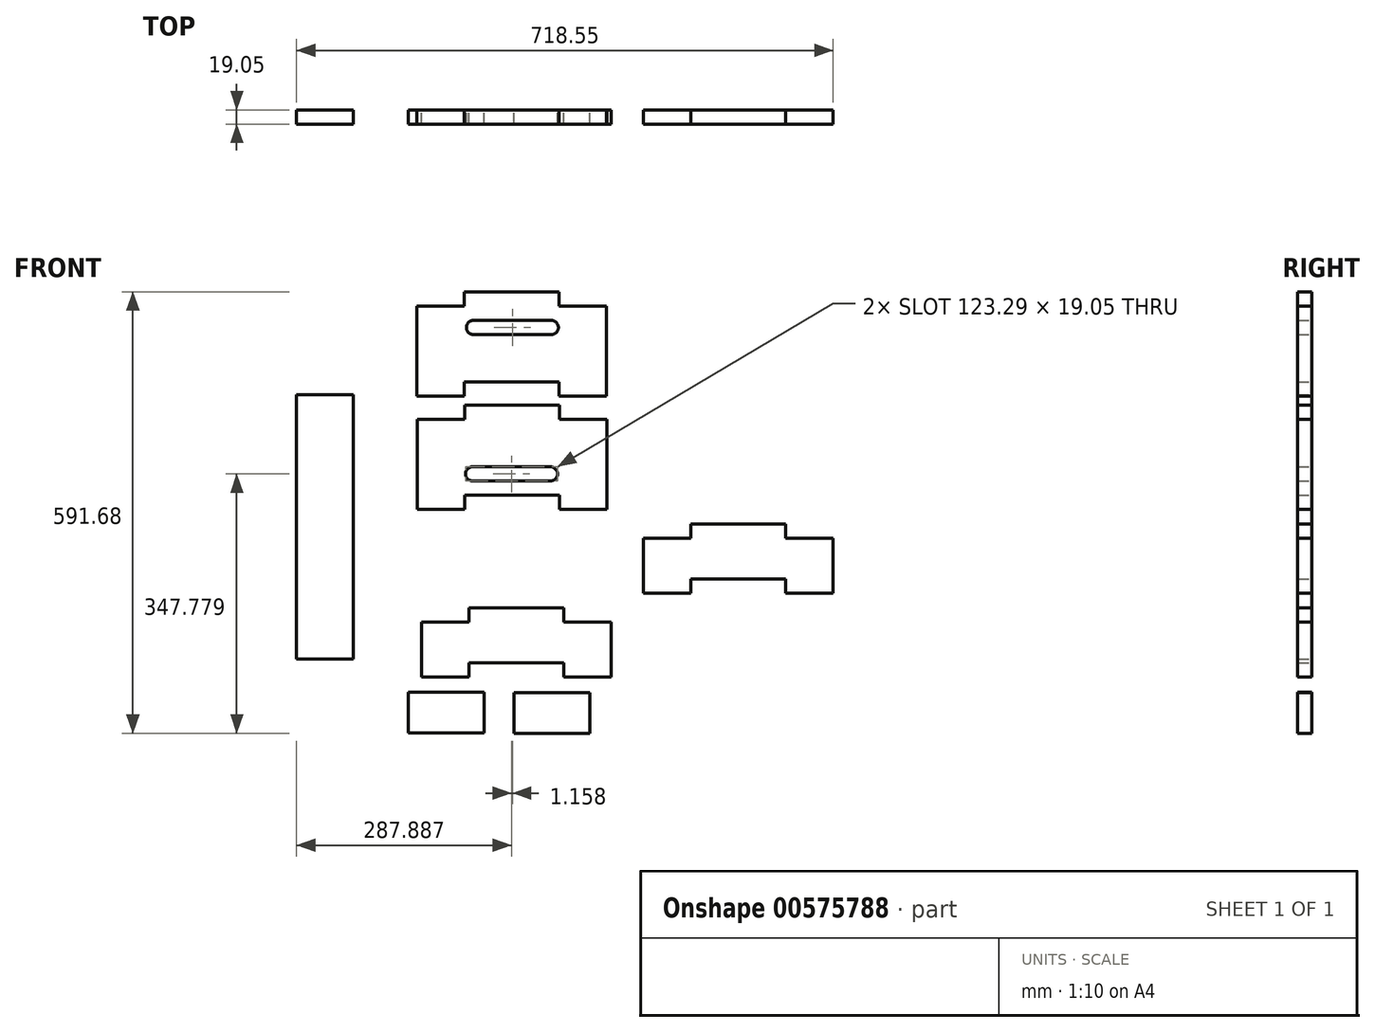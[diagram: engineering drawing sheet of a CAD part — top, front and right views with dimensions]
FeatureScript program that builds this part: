
annotation { "Feature Type Name" : "Feature", "Feature Type Description" : "" }
export const myFeature = defineFeature(function(context is Context, id is Id, definition is map)
    precondition{}
    {
        {
            var Q0;
            Q0=qCreatedBy(makeId("Front.planeOp"),FACE);
            var sketch = newSketch(context, id + "F0", { "sketchPlane" : qUnion([Q0])});
            skLineSegment(sketch, "E0", {"start": v(-218.52, -88.37) * mm, "end": v(-142.32, -88.37) * mm});
            skLineSegment(sketch, "E1", {"start": v(-142.32, -88.37) * mm, "end": v(-142.32, 265.96) * mm});
            skLineSegment(sketch, "E2", {"start": v(-142.32, 265.96) * mm, "end": v(-218.52, 265.96) * mm});
            skLineSegment(sketch, "E3", {"start": v(-218.52, 265.96) * mm, "end": v(-218.52, -88.37) * mm});
            skLineSegment(sketch, "E4", {"start": v(72.53, -133.52) * mm, "end": v(174.13, -133.52) * mm});
            skLineSegment(sketch, "E5", {"start": v(174.13, -133.52) * mm, "end": v(174.13, -188.13) * mm});
            skLineSegment(sketch, "E6", {"start": v(174.13, -188.13) * mm, "end": v(72.53, -188.13) * mm});
            skLineSegment(sketch, "E7", {"start": v(72.53, -188.13) * mm, "end": v(72.53, -133.52) * mm});
            skLineSegment(sketch, "E8", {"start": v(-68.87, -133.16) * mm, "end": v(32.73, -133.16) * mm});
            skLineSegment(sketch, "E9", {"start": v(32.73, -133.16) * mm, "end": v(32.73, -187.77) * mm});
            skLineSegment(sketch, "E10", {"start": v(32.73, -187.77) * mm, "end": v(-68.87, -187.77) * mm});
            skLineSegment(sketch, "E11", {"start": v(-68.87, -187.77) * mm, "end": v(-68.87, -133.16) * mm});
            skLineSegment(sketch, "E12", {"start": v(202.7, -39.13) * mm, "end": v(202.7, -112.79) * mm});
            skLineSegment(sketch, "E13", {"start": v(-51.3, -112.79) * mm, "end": v(-51.3, -39.13) * mm});
            skLineSegment(sketch, "E14", {"start": v(-51.3, -39.13) * mm, "end": v(12.2, -39.13) * mm});
            skLineSegment(sketch, "E15", {"start": v(12.2, -39.13) * mm, "end": v(12.2, -20.08) * mm});
            skLineSegment(sketch, "E16", {"start": v(12.2, -20.08) * mm, "end": v(139.2, -20.08) * mm});
            skLineSegment(sketch, "E17", {"start": v(139.2, -20.08) * mm, "end": v(139.2, -39.13) * mm});
            skLineSegment(sketch, "E18", {"start": v(139.2, -39.13) * mm, "end": v(202.7, -39.13) * mm});
            skLineSegment(sketch, "E19", {"start": v(-51.3, -112.79) * mm, "end": v(12.2, -112.79) * mm});
            skLineSegment(sketch, "E20", {"start": v(12.2, -112.79) * mm, "end": v(12.2, -93.74) * mm});
            skLineSegment(sketch, "E21", {"start": v(12.2, -93.74) * mm, "end": v(139.2, -93.74) * mm});
            skLineSegment(sketch, "E22", {"start": v(139.2, -93.74) * mm, "end": v(139.2, -112.79) * mm});
            skLineSegment(sketch, "E23", {"start": v(139.2, -112.79) * mm, "end": v(202.7, -112.79) * mm});
            skLineSegment(sketch, "E24", {"start": v(500.03, 73.66) * mm, "end": v(500.03, 0) * mm});
            skLineSegment(sketch, "E25", {"start": v(246.03, 0) * mm, "end": v(246.03, 73.66) * mm});
            skLineSegment(sketch, "E26", {"start": v(246.03, 73.66) * mm, "end": v(309.53, 73.66) * mm});
            skLineSegment(sketch, "E27", {"start": v(309.53, 73.66) * mm, "end": v(309.53, 92.7) * mm});
            skLineSegment(sketch, "E28", {"start": v(309.53, 92.7) * mm, "end": v(436.53, 92.7) * mm});
            skLineSegment(sketch, "E29", {"start": v(436.53, 92.7) * mm, "end": v(436.53, 73.66) * mm});
            skLineSegment(sketch, "E30", {"start": v(436.53, 73.66) * mm, "end": v(500.03, 73.66) * mm});
            skLineSegment(sketch, "E31", {"start": v(246.03, 0) * mm, "end": v(309.53, 0) * mm});
            skLineSegment(sketch, "E32", {"start": v(309.53, 0) * mm, "end": v(309.53, 19.05) * mm});
            skLineSegment(sketch, "E33", {"start": v(309.53, 19.05) * mm, "end": v(436.53, 19.05) * mm});
            skLineSegment(sketch, "E34", {"start": v(436.53, 19.05) * mm, "end": v(436.53, 0) * mm});
            skLineSegment(sketch, "E35", {"start": v(436.53, 0) * mm, "end": v(500.03, 0) * mm});
            skLineSegment(sketch, "E36", {"start": v(197.32, 232.67) * mm, "end": v(197.32, 112.02) * mm});
            skLineSegment(sketch, "E37", {"start": v(-56.68, 112.02) * mm, "end": v(-56.68, 232.67) * mm});
            skLineSegment(sketch, "E38", {"start": v(-56.68, 232.67) * mm, "end": v(6.82, 232.67) * mm});
            skLineSegment(sketch, "E39", {"start": v(6.82, 232.67) * mm, "end": v(6.82, 251.72) * mm});
            skLineSegment(sketch, "E40", {"start": v(6.82, 251.72) * mm, "end": v(133.82, 251.72) * mm});
            skLineSegment(sketch, "E41", {"start": v(133.82, 251.72) * mm, "end": v(133.82, 232.67) * mm});
            skLineSegment(sketch, "E42", {"start": v(133.82, 232.67) * mm, "end": v(197.32, 232.67) * mm});
            skLineSegment(sketch, "E43", {"start": v(-56.68, 112.02) * mm, "end": v(6.82, 112.02) * mm});
            skLineSegment(sketch, "E44", {"start": v(6.82, 112.02) * mm, "end": v(6.82, 131.07) * mm});
            skLineSegment(sketch, "E45", {"start": v(6.82, 131.07) * mm, "end": v(133.82, 131.07) * mm});
            skLineSegment(sketch, "E46", {"start": v(133.82, 131.07) * mm, "end": v(133.82, 112.02) * mm});
            skLineSegment(sketch, "E47", {"start": v(133.82, 112.02) * mm, "end": v(197.32, 112.02) * mm});
            skLineSegment(sketch, "E48", {"start": v(17.25, 169.17) * mm, "end": v(121.49, 169.17) * mm});
            skLineSegment(sketch, "E49", {"start": v(121.49, 150.12) * mm, "end": v(17.25, 150.12) * mm});
            skArc(sketch, "E50", {"start": v(17.25, 169.17) * mm, "mid": v(7.72, 159.65) * mm, "end": v(17.25, 150.12) * mm});
            skArc(sketch, "E51", {"start": v(121.49, 150.12) * mm, "mid": v(131.01, 159.65) * mm, "end": v(121.49, 169.17) * mm});
            skLineSegment(sketch, "E52", {"start": v(196.61, 384.5) * mm, "end": v(196.61, 263.85) * mm});
            skLineSegment(sketch, "E53", {"start": v(-57.39, 263.85) * mm, "end": v(-57.39, 384.5) * mm});
            skLineSegment(sketch, "E54", {"start": v(-57.39, 384.5) * mm, "end": v(6.11, 384.5) * mm});
            skLineSegment(sketch, "E55", {"start": v(6.11, 384.5) * mm, "end": v(6.11, 403.55) * mm});
            skLineSegment(sketch, "E56", {"start": v(6.11, 403.55) * mm, "end": v(133.11, 403.55) * mm});
            skLineSegment(sketch, "E57", {"start": v(133.11, 403.55) * mm, "end": v(133.11, 384.5) * mm});
            skLineSegment(sketch, "E58", {"start": v(133.11, 384.5) * mm, "end": v(196.61, 384.5) * mm});
            skLineSegment(sketch, "E59", {"start": v(-57.39, 263.85) * mm, "end": v(6.11, 263.85) * mm});
            skLineSegment(sketch, "E60", {"start": v(6.11, 263.85) * mm, "end": v(6.11, 282.9) * mm});
            skLineSegment(sketch, "E61", {"start": v(6.11, 282.9) * mm, "end": v(133.11, 282.9) * mm});
            skLineSegment(sketch, "E62", {"start": v(133.11, 282.9) * mm, "end": v(133.11, 263.85) * mm});
            skLineSegment(sketch, "E63", {"start": v(133.11, 263.85) * mm, "end": v(196.61, 263.85) * mm});
            skLineSegment(sketch, "E64", {"start": v(18.4, 365.45) * mm, "end": v(122.65, 365.45) * mm});
            skLineSegment(sketch, "E65", {"start": v(122.65, 346.4) * mm, "end": v(18.4, 346.4) * mm});
            skArc(sketch, "E66", {"start": v(18.4, 365.45) * mm, "mid": v(8.88, 355.93) * mm, "end": v(18.4, 346.4) * mm});
            skArc(sketch, "E67", {"start": v(122.65, 346.4) * mm, "mid": v(132.17, 355.93) * mm, "end": v(122.65, 365.45) * mm});
            skSolve(sketch);
        }
        {
            var Q0;
            Q0=makeQuery(id+"F0.imprint","IMPRINT",FACE,{"disambiguationData":[TD([[makeQuery(id+"F0.imprint","IMPRINT",EDGE,{"derivedFrom":sQuery(id+"F0.wireOp",EDGE,"E0")}),1.0]])]});
            extrude(context, id + "F1", {"entities" : qUnion([Q0]), "depth" : 19.05 * mm, "offsetDistance" : 25.4 * mm});
        }
        {
            var Q0;
            Q0=makeQuery(id+"F0.imprint","IMPRINT",FACE,{"disambiguationData":[TD([[makeQuery(id+"F0.imprint","IMPRINT",EDGE,{"derivedFrom":sQuery(id+"F0.wireOp",EDGE,"E52")}),-1.0]])]});
            var Q1;
            Q1=makeQuery(id+"F0.imprint","IMPRINT",FACE,{"disambiguationData":[TD([[makeQuery(id+"F0.imprint","IMPRINT",EDGE,{"derivedFrom":sQuery(id+"F0.wireOp",EDGE,"E36")}),-1.0]])]});
            var Q2;
            Q2=makeQuery(id+"F0.imprint","IMPRINT",FACE,{"disambiguationData":[TD([[makeQuery(id+"F0.imprint","IMPRINT",EDGE,{"derivedFrom":sQuery(id+"F0.wireOp",EDGE,"E24")}),-1.0]])]});
            var Q3;
            Q3=makeQuery(id+"F0.imprint","IMPRINT",FACE,{"disambiguationData":[TD([[makeQuery(id+"F0.imprint","IMPRINT",EDGE,{"derivedFrom":sQuery(id+"F0.wireOp",EDGE,"E12")}),-1.0]])]});
            var Q4;
            Q4=makeQuery(id+"F0.imprint","IMPRINT",FACE,{"disambiguationData":[TD([[makeQuery(id+"F0.imprint","IMPRINT",EDGE,{"derivedFrom":sQuery(id+"F0.wireOp",EDGE,"E4")}),-1.0]])]});
            var Q5;
            Q5=makeQuery(id+"F0.imprint","IMPRINT",FACE,{"disambiguationData":[TD([[makeQuery(id+"F0.imprint","IMPRINT",EDGE,{"derivedFrom":sQuery(id+"F0.wireOp",EDGE,"E8")}),-1.0]])]});
            extrude(context, id + "F2", {"entities" : qUnion([Q0, Q1, Q2, Q3, Q4, Q5]), "depth" : 19.05 * mm, "offsetDistance" : 25.4 * mm});
        }
    });
